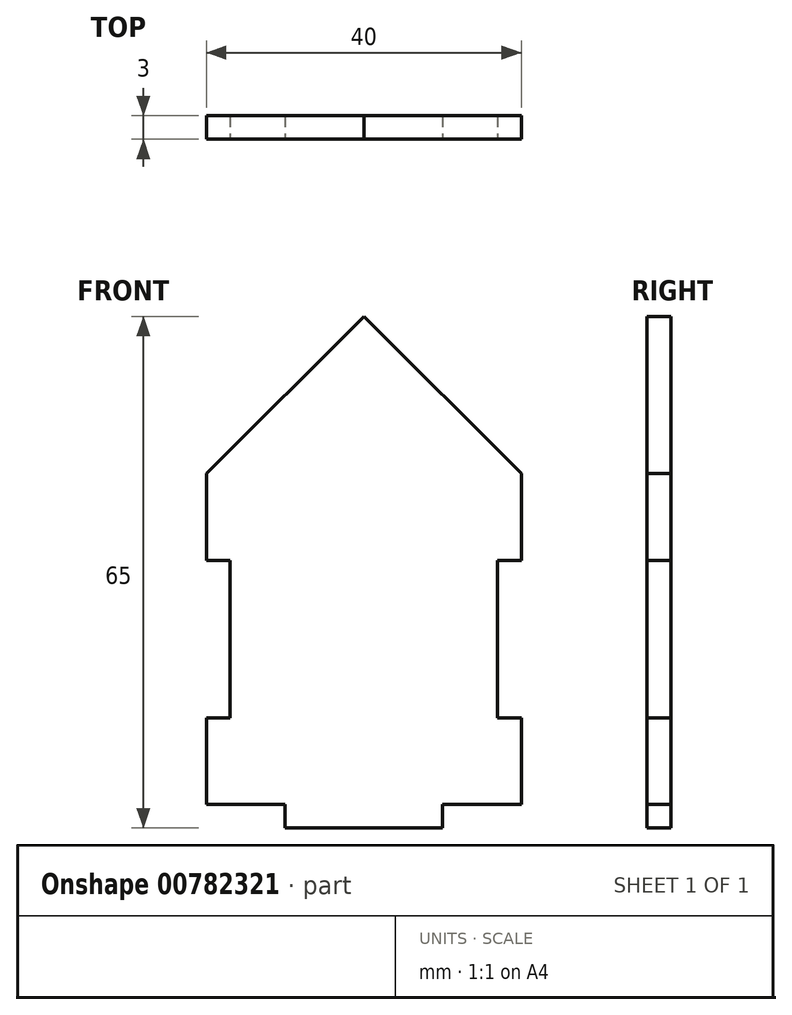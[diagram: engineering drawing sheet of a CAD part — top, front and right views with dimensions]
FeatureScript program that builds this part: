
annotation { "Feature Type Name" : "Feature", "Feature Type Description" : "" }
export const myFeature = defineFeature(function(context is Context, id is Id, definition is map)
    precondition{}
    {
        {
            var Q0;
            Q0=qCreatedBy(makeId("Front.planeOp"),FACE);
            var sketch = newSketch(context, id + "F0", { "sketchPlane" : qUnion([Q0])});
            skLineSegment(sketch, "E0.top", {"start": v(20, -21) * mm, "end": v(-20, -21) * mm});
            skPoint(sketch, "E0.middle", {"position": v(0, 0) * mm});
            skLineSegment(sketch, "E1", {"start": v(-20, 21) * mm, "end": v(0, 41) * mm});
            skLineSegment(sketch, "E2", {"start": v(0, 41) * mm, "end": v(20, 21) * mm});
            skLineSegment(sketch, "E3", {"start": v(-20, 10) * mm, "end": v(-17, 10) * mm});
            skLineSegment(sketch, "E4", {"start": v(-17, 10) * mm, "end": v(-17, -10) * mm});
            skLineSegment(sketch, "E5", {"start": v(-17, -10) * mm, "end": v(-20, -10) * mm});
            skLineSegment(sketch, "E6", {"start": v(-20, 21) * mm, "end": v(-20, 10) * mm});
            skLineSegment(sketch, "E7", {"start": v(-20, -10) * mm, "end": v(-20, -21) * mm});
            skLineSegment(sketch, "E8", {"start": v(20, 21) * mm, "end": v(20, 10) * mm});
            skLineSegment(sketch, "E9", {"start": v(20, 10) * mm, "end": v(17, 10) * mm});
            skLineSegment(sketch, "E10", {"start": v(17, 10) * mm, "end": v(17, -10) * mm});
            skLineSegment(sketch, "E11", {"start": v(17, -10) * mm, "end": v(20, -10) * mm});
            skLineSegment(sketch, "E12", {"start": v(20, -10) * mm, "end": v(20, -21) * mm});
            skLineSegment(sketch, "E13", {"start": v(-10, -21) * mm, "end": v(-10, -24) * mm});
            skLineSegment(sketch, "E14", {"start": v(-10, -24) * mm, "end": v(10, -24) * mm});
            skLineSegment(sketch, "E15", {"start": v(10, -24) * mm, "end": v(10, -21) * mm});
            skSolve(sketch);
        }
        {
            var Q0;
            Q0=makeQuery(id+"F0.imprint","IMPRINT",FACE,{"disambiguationData":[TD([[makeQuery(id+"F0.imprint","IMPRINT",EDGE,{"derivedFrom":sQuery(id+"F0.wireOp",EDGE,"E3")}),1.0]])]});
            var Q1;
            {var subQ0=sQuery(id+"F0.wireOp",EDGE,"c90049ba-afea-4f03-8b41-77b7b003ae6d0.MirrorCS");Q1=makeQuery(id+"F0.imprint","IMPRINT",FACE,{"disambiguationData":[TD([[makeQuery(id+"F0.imprint","IMPRINT",EDGE,{"derivedFrom":subQ0}),1.0]])]});}
            var Q2;
            {var subQ0=sQuery(id+"F0.wireOp",EDGE,"Lv1DZn4h-48uY-n0iO-hpn6-IClfQAFSjkQm");Q2=makeQuery(id+"F0.imprint","IMPRINT",FACE,{"disambiguationData":[TD([[makeQuery(id+"F0.imprint","IMPRINT",EDGE,{"derivedFrom":subQ0}),-1.0]])]});}
            var Q3;
            {var subQ0=sQuery(id+"F0.wireOp",EDGE,"E13");Q3=makeQuery(id+"F0.imprint","IMPRINT",FACE,{"disambiguationData":[TD([[makeQuery(id+"F0.imprint","IMPRINT",EDGE,{"derivedFrom":subQ0}),1.0]])]});}
            extrude(context, id + "F1", {"entities" : qUnion([Q0, Q1, Q2, Q3]), "oppositeDirection" : true, "depth" : 3 * mm, "offsetDistance" : 25 * mm});
        }
    });
